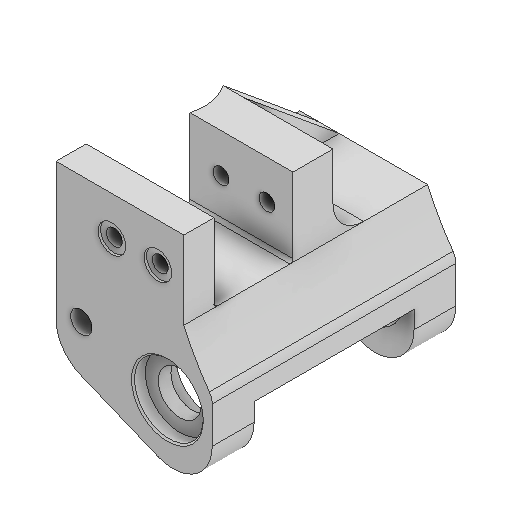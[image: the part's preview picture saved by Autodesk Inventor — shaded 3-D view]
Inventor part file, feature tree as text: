
AUTODESK INVENTOR PART (.ipt)
format: ipt  version: 2025 (Build 290162000, 162)  size: 547,840 bytes
history: native  units: in
note: dims shown in document units (in); Inventor stores cm internally (conversion verified against a paired STEP export)
features: extrude x19, sketch x19, projected_geometry x13, fillet x9, reference x3, other x3, mirror x2, chamfer x2, thicken_offset x1, plane x1
ambient origin geometry x8: Origin, YZ Plane, XZ Plane, XY Plane, X Axis, Y Axis, Z Axis, Center Point
bodies: Solid1 (feature_tree)
feature tree (72):
  extrude  "Extrusion1"  Depth=0.25in
  extrude  "Extrusion2"  Depth=2.0in
  extrude  "Extrusion7"  Depth=0.8809in
  extrude  "Extrusion10"  Depth=0.2165in TaperAngle=0.0deg
  extrude  "Extrusion11"  Depth=0.315in
  extrude  "Extrusion12"  TaperAngle=0.0deg  [1 undecoded]
  extrude  "Extrusion13"  Depth=0.3937in TaperAngle=0.0deg
  mirror  "Mirror1"
  fillet  "Fillet5"  Radius=0.3937in
  extrude  "Extrusion14"  Depth=0.3937in
  fillet  "Fillet6"  [1 undecoded]
  extrude  "Extrusion15"  Depth=0.3937in
  thicken_offset  "Thicken1"
  fillet  "Fillet7"  Radius=0.3858in
  extrude  "Extrusion16"  Depth=0.5118in
  extrude  "Extrusion17"  Depth=0.1969in
  fillet  "Fillet8"  Radius=1.0in
  extrude  "Extrusion18"  Depth=0.3937in
  extrude  "Extrusion19"  Depth=1.0in TaperAngle=0.0deg
  extrude  "Extrusion20"  Depth=0.315in
  extrude  "Extrusion21"  Depth=0.3228in
  extrude  "Extrusion22"  Depth=0.2756in
  extrude  "Extrusion23"  Depth=0.2047in
  plane  "Work Plane1"
  mirror  "Mirror2"
  fillet  "Fillet9"  Radius=0.2047in
  fillet  "Fillet10"  [1 undecoded]
  fillet  "Fillet11"  Radius=0.3543in
  extrude  "Extrusion24"  Depth=0.315in TaperAngle=0.0deg
  extrude  "Extrusion25"  Depth=0.5in
  fillet  "Fillet12"  Radius=0.0394in
  fillet  "Fillet13"  Radius=0.1969in
  chamfer  "Chamfer1"  [1 undecoded]
  chamfer  "Chamfer2"  Distance=0.5in
  sketch  "Sketch1"  dims[d1=1.005in d2=0.25in]
  sketch  "Sketch2"  dims[d3=2.0in d4=0.0in d5=0.5512in]
  projected_geometry  "Projected Loop1"
  sketch  "Sketch7"  dims[d6=0.0in d7=0.0in d21=0.8809in]
  sketch  "Sketch10"  dims[d22=0.1575in d23=0.0in d32=0.2165in d33=0.0in]
  projected_geometry  "Projected Loop7"
  sketch  "Sketch11"  dims[d34=1.1024in d35=0.315in]
  sketch  "Sketch12"  dims[d36=0.2047in d37=0.0in d38=0.0in]
  projected_geometry  "Projected Loop8"
  sketch  "Sketch13"  dims[d39=0.3937in d40=0.0in d42=1.0236in d43=0.0in d45=0.3937in]
  projected_geometry  "Projected Loop9"
  sketch  "Sketch14"  dims[d46=1.0236in d47=0.0in d48=0.3937in d49=0.0in d50=0.0in]
  projected_geometry  "Projected Loop10"
  sketch  "Sketch15"  dims[d51=0.0591in d52=0.1in d53=0.3937in d54=0.3858in]
  projected_geometry  "Projected Loop11"
  sketch  "Sketch16"  dims[d55=0.0079in d56=0.5118in]
  projected_geometry  "Projected Loop12"
  reference  "Reference1"
  sketch  "Sketch17"  dims[d57=0.2756in d58=0.1969in d59=1.0in d60=0.0in]
  projected_geometry  "Projected Loop13"
  sketch  "Sketch18"  dims[d61=1.0in d62=0.0in d63=0.3937in]
  projected_geometry  "Projected Loop14"
  reference  "Reference2"
  sketch  "Sketch19"  dims[d64=0.2047in d65=1.0in d66=0.0in]
  sketch  "Sketch20"  dims[d67=0.315in d68=0.315in]
  sketch  "Sketch21"  dims[d69=0.1969in d70=0.0in d71=0.3228in]
  sketch  "Sketch22"  dims[d72=0.315in d73=0.0in d74=0.2756in]
  reference  "Reference3"
  sketch  "Sketch23"  dims[d75=0.4724in d76=0.0in d77=0.2047in d78=0.2047in d79=0.0in d80=0.0in d81=0.3543in]
  projected_geometry  "Projected Loop15"
  sketch  "Sketch24"  dims[d82=0.3543in d83=0.315in d84=0.0in]
  projected_geometry  "Projected Loop16"
  projected_geometry  "Projected Loop17"
  sketch  "Sketch25"  dims[d85=0.7874in d86=0.1969in d87=0.0394in d88=0.1969in d89=0.0in d90=0.0in d91=0.0in d92=0.5in d93=0.5in d94=0.0197in d95=0.0787in d96=45.0deg d97=0.1181in d98=0.0787in d99=45.0deg d24=0.0344in d27=0.0in d28=0.0in d29=0.0in d30=0.0in]
  projected_geometry  "Projected Loop18"
  other  "<userpath>\Desktop\puppycat\singleSwingarmV2.iam"
  other  "singleSwingarmV2.iam"
  other  "trackBase:1"
note: 4 required parameter values undecoded (feature->parameter linkage not recoverable at this tier; creation-order binding heuristic only, values carry confidence <= 0.55)
